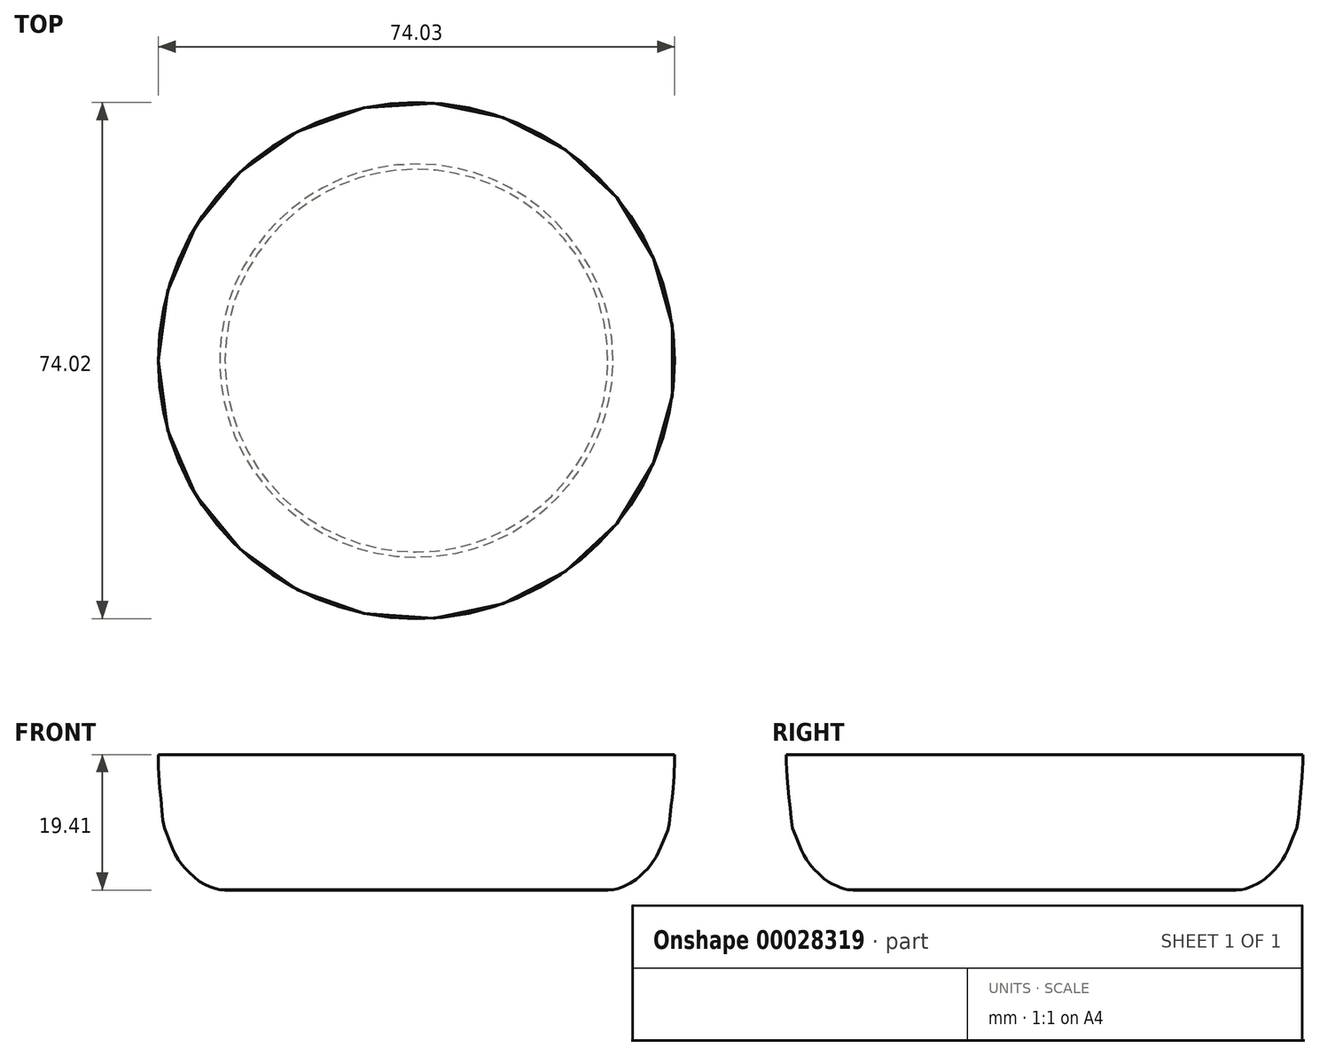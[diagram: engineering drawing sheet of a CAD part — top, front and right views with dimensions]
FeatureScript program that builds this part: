
annotation { "Feature Type Name" : "Feature", "Feature Type Description" : "" }
export const myFeature = defineFeature(function(context is Context, id is Id, definition is map)
    precondition{}
    {
        {
            var Q0;
            Q0=qCreatedBy(makeId("Front.planeOp"),FACE);
            var sketch = newSketch(context, id + "F0", { "sketchPlane" : qUnion([Q0])});
            skLineSegment(sketch, "E0", {"start": v(-32.18, 3.08) * mm, "end": v(41.82, 3.08) * mm});
            skPoint(sketch, "E1", {"position": v(4.82, 3.08) * mm});
            skLineSegment(sketch, "E2", {"start": v(4.82, -19.82) * mm, "end": v(4.82, 49.92) * mm, "construction": true});
            skLineSegment(sketch, "E3", {"start": v(4.82, -16.33) * mm, "end": v(32.26, -16.33) * mm});
            skFitSpline(sketch, "E4", {"points": [v(33, -16.26) * mm, v(33.61, -16.13) * mm, v(34.39, -15.85) * mm, v(35.18, -15.5) * mm, v(36.15, -14.92) * mm, v(37.03, -14.16) * mm, v(37.8, -13.4) * mm, v(38.32, -12.84) * mm, v(38.84, -12.12) * mm, v(39.39, -11.24) * mm, v(39.87, -10.14) * mm, v(40.4, -8.8) * mm, v(40.96, -7.41) * mm, v(41.22, -5.45) * mm, v(41.57, -2.01) * mm, v(41.7, -0.53) * mm, v(41.79, 0.85) * mm, v(41.83, 2.12) * mm, v(41.82, 3.08) * mm], "startDerivative": vector(15.4, 2.64) * mm, "endDerivative": vector(-1.1, 16.45) * mm});
            skLineSegment(sketch, "E5", {"start": v(32.26, -16.33) * mm, "end": v(33, -16.26) * mm});
            skLineSegment(sketch, "E6", {"start": v(4.82, -16.33) * mm, "end": v(4.82, 3.08) * mm});
            skSolve(sketch);
        }
        {
            var Q0;
            Q0=makeQuery(id+"F0.imprint","IMPRINT",FACE,{"disambiguationData":[TD([[makeQuery(id+"F0.imprint","IMPRINT",EDGE,{"derivedFrom":sQuery(id+"F0.wireOp",EDGE,"E3")}),1.0]])]});
            var Q1;
            Q1=sQuery(id+"F0.wireOp",EDGE,"E2");
            revolve(context, id + "F1", {"entities" : qUnion([Q0]), "axis" : qUnion([Q1]), "revolveType" : RevolveType.FULL});
        }
    });
